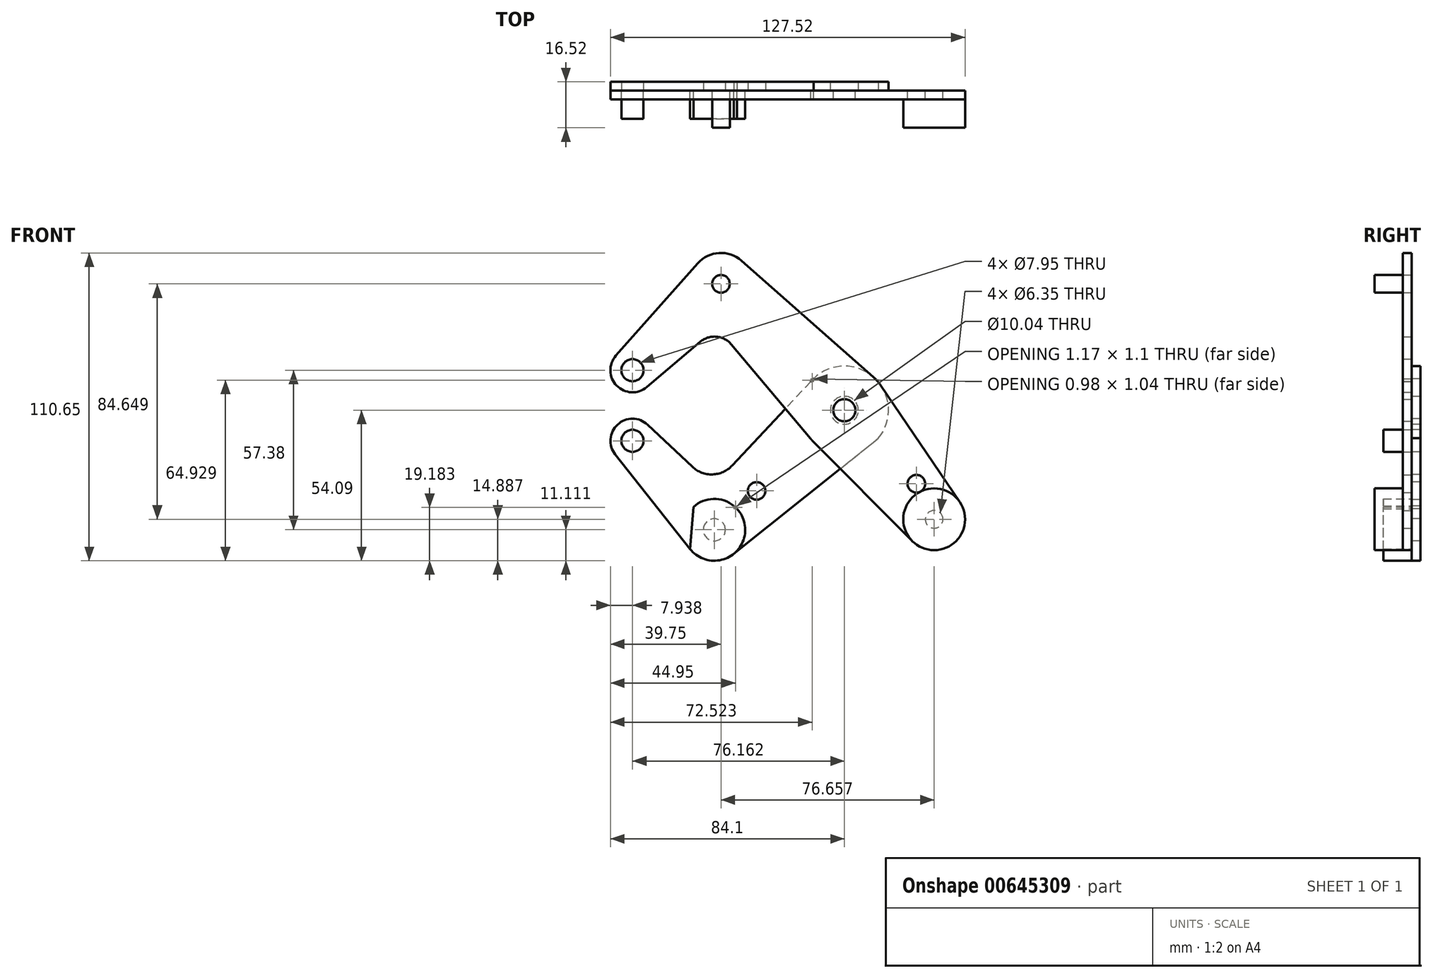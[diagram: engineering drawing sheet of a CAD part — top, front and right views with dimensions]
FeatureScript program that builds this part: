
annotation { "Feature Type Name" : "Feature", "Feature Type Description" : "" }
export const myFeature = defineFeature(function(context is Context, id is Id, definition is map)
    precondition{}
    {
        {
            var Q0;
            Q0=qCreatedBy(makeId("Front.planeOp"),FACE);
            var sketch = newSketch(context, id + "F0", { "sketchPlane" : qUnion([Q0])});
            skCircle(sketch, "E0", {"center": v(-76.16, 14.4) * mm, "radius": 7.94 * mm});
            skLineSegment(sketch, "E1", {"start": v(-76.16, 14.4) * mm, "end": v(-44.35, 45.45) * mm, "construction": true});
            skCircle(sketch, "E2", {"center": v(-44.35, 45.45) * mm, "radius": 3.18 * mm});
            skCircle(sketch, "E3", {"center": v(-44.35, 45.45) * mm, "radius": 11.11 * mm});
            skLineSegment(sketch, "E4", {"start": v(-44.35, 45.45) * mm, "end": v(0, 0) * mm, "construction": true});
            skCircle(sketch, "E5", {"center": v(0, 0) * mm, "radius": 15.88 * mm});
            skCircle(sketch, "E6", {"center": v(0, 0) * mm, "radius": 3.98 * mm});
            skCircle(sketch, "E7", {"center": v(-76.16, 14.4) * mm, "radius": 3.98 * mm});
            skCircle(sketch, "E8", {"center": v(0, 0) * mm, "radius": 5.02 * mm});
            skLineSegment(sketch, "E9", {"start": v(-82.1, 19.67) * mm, "end": v(-52.66, 52.82) * mm});
            skLineSegment(sketch, "E10", {"start": v(-71.04, 8.34) * mm, "end": v(-51.79, 24.6) * mm});
            skLineSegment(sketch, "E11", {"start": v(-40.57, 23.65) * mm, "end": v(-12.16, -10.2) * mm});
            skLineSegment(sketch, "E12", {"start": v(10.5, 11.9) * mm, "end": v(-37, 53.78) * mm});
            skLineSegment(sketch, "E13", {"start": v(0, 0) * mm, "end": v(32.3, -39.2) * mm, "construction": true});
            skCircle(sketch, "E14", {"center": v(32.3, -39.2) * mm, "radius": 11.11 * mm});
            skCircle(sketch, "E15", {"center": v(25.9, -26.43) * mm, "radius": 3.18 * mm});
            skCircle(sketch, "E16", {"center": v(32.3, -39.2) * mm, "radius": 3.18 * mm});
            skLineSegment(sketch, "E17", {"start": v(13.14, 8.9) * mm, "end": v(41.5, -32.97) * mm});
            skLineSegment(sketch, "E18", {"start": v(-11.25, -11.2) * mm, "end": v(24.43, -47.04) * mm});
            skArc(sketch, "E19", {"start": v(-40.57, 23.65) * mm, "mid": v(-45.98, 26.46) * mm, "end": v(-51.79, 24.6) * mm});
            skLineSegment(sketch, "E20.trimOffspring", {"start": v(-37.18, 36.96) * mm, "end": v(-36.57, 37.47) * mm});
            skLineSegment(sketch, "E21", {"start": v(0, 0) * mm, "end": v(-46.74, -42.98) * mm, "construction": true});
            skLineSegment(sketch, "E22", {"start": v(-46.74, -42.98) * mm, "end": v(-76.16, -10.98) * mm, "construction": true});
            skCircle(sketch, "E23", {"center": v(-76.16, -10.98) * mm, "radius": 7.94 * mm});
            skCircle(sketch, "E24", {"center": v(-76.16, -10.98) * mm, "radius": 3.98 * mm});
            skCircle(sketch, "E25", {"center": v(-46.74, -42.98) * mm, "radius": 11.11 * mm});
            skCircle(sketch, "E26", {"center": v(-46.74, -42.98) * mm, "radius": 3.98 * mm});
            skCircle(sketch, "E27", {"center": v(-31.54, -29) * mm, "radius": 3.18 * mm});
            skLineSegment(sketch, "E28", {"start": v(-70.72, -5.2) * mm, "end": v(-54.64, -20.33) * mm});
            skLineSegment(sketch, "E29", {"start": v(-39.8, -51.66) * mm, "end": v(12.27, -10.07) * mm});
            skLineSegment(sketch, "E30", {"start": v(-11.09, 11.36) * mm, "end": v(-40.34, -19.88) * mm});
            skArc(sketch, "E31", {"start": v(-54.64, -20.33) * mm, "mid": v(-47.4, -23.07) * mm, "end": v(-40.34, -19.88) * mm});
            skLineSegment(sketch, "E32.trimOffspring", {"start": v(-39.74, -34.36) * mm, "end": v(-38.56, -35.46) * mm});
            skLineSegment(sketch, "E33", {"start": v(-55.45, -49.88) * mm, "end": v(-82.38, -15.92) * mm});
            skLineSegment(sketch, "E34", {"start": v(-76.16, 14.4) * mm, "end": v(-76.16, -10.98) * mm, "construction": true});
            skLineSegment(sketch, "E35", {"start": v(-55.45, -49.88) * mm, "end": v(-54.27, -34.8) * mm});
            skSolve(sketch);
        }
        {
            var Q0;
            Q0=makeQuery(id+"F0.imprint","IMPRINT",FACE,{"disambiguationData":[TD([[makeQuery(id+"F0.imprint","IMPRINT",EDGE,{"derivedFrom":sQuery(id+"F0.wireOp",EDGE,"E7")}),-1.0]])]});
            var Q1;
            {var subQ1=sQuery(id+"F0.wireOp",EDGE,"E9");Q1=makeQuery(id+"F0.imprint","IMPRINT",FACE,{"disambiguationData":[TD([[makeQuery(id+"F0.imprint","IMPRINT",EDGE,{"derivedFrom":subQ1}),-1.0]])]});}
            var Q2;
            Q2=makeQuery(id+"F0.imprint","IMPRINT",FACE,{"disambiguationData":[TD([[makeQuery(id+"F0.imprint","IMPRINT",EDGE,{"derivedFrom":sQuery(id+"F0.wireOp",EDGE,"E2")}),-1.0]])]});
            var Q3;
            {var subQ0=sQuery(id+"F0.wireOp",EDGE,"E11");var subQ1=sQuery(id+"F0.wireOp",EDGE,"E5");var subQ2=makeQuery(id+"F0.imprint","INTERSECT",VERTEX,{"derivedFrom":[subQ1,subQ0]});Q3=makeQuery(id+"F0.imprint","IMPRINT",FACE,{"disambiguationData":[TD([[makeQuery(id+"F0.imprint","IMPRINT",EDGE,{"disambiguationData":[TD([[subQ2,1.0]])],"derivedFrom":subQ1}),-1.0]])]});}
            var Q4;
            {var subQ0=sQuery(id+"F0.wireOp",EDGE,"E18");var subQ1=sQuery(id+"F0.wireOp",EDGE,"E5");var subQ2=makeQuery(id+"F0.imprint","INTERSECT",VERTEX,{"derivedFrom":[subQ1,subQ0]});Q4=makeQuery(id+"F0.imprint","IMPRINT",FACE,{"disambiguationData":[TD([[makeQuery(id+"F0.imprint","IMPRINT",EDGE,{"disambiguationData":[TD([[subQ2,-1.0]])],"derivedFrom":subQ1}),-1.0]])]});}
            var Q5;
            {var subQ3=sQuery(id+"F0.wireOp",EDGE,"E15");Q5=makeQuery(id+"F0.imprint","IMPRINT",FACE,{"disambiguationData":[TD([[makeQuery(id+"F0.imprint","IMPRINT",EDGE,{"derivedFrom":subQ3}),-1.0]])]});}
            var Q6;
            Q6=makeQuery(id+"F0.imprint","IMPRINT",FACE,{"disambiguationData":[TD([[makeQuery(id+"F0.imprint","IMPRINT",EDGE,{"derivedFrom":sQuery(id+"F0.wireOp",EDGE,"E6")}),-1.0]])]});
            var Q7;
            Q7=makeQuery(id+"F0.imprint","IMPRINT",FACE,{"disambiguationData":[TD([[makeQuery(id+"F0.imprint","IMPRINT",EDGE,{"derivedFrom":sQuery(id+"F0.wireOp",EDGE,"E16")}),-1.0]])]});
            var Q8;
            {var subQ0=sQuery(id+"F0.wireOp",EDGE,"E29");var subQ1=sQuery(id+"F0.wireOp",EDGE,"E5");var subQ2=makeQuery(id+"F0.imprint","INTERSECT",VERTEX,{"disambiguationData":[OD(0.0)],"derivedFrom":[subQ1,subQ0]});Q8=makeQuery(id+"F0.imprint","IMPRINT",FACE,{"disambiguationData":[TD([[makeQuery(id+"F0.imprint","IMPRINT",EDGE,{"disambiguationData":[TD([[subQ2,1.0]])],"derivedFrom":subQ1}),1.0]])]});}
            var Q9;
            Q9=makeQuery(id+"F0.imprint","IMPRINT",FACE,{"disambiguationData":[TD([[makeQuery(id+"F0.imprint","IMPRINT",EDGE,{"derivedFrom":sQuery(id+"F0.wireOp",EDGE,"E8")}),-1.0]])]});
            extrude(context, id + "F1", {"entities" : qUnion([Q0, Q1, Q2, Q3, Q4, Q5, Q6, Q7, Q8, Q9]), "depth" : 3.17 * mm, "offsetDistance" : 25.4 * mm});
        }
        {
            var Q0;
            Q0=makeQuery(id+"F0.imprint","IMPRINT",FACE,{"disambiguationData":[TD([[makeQuery(id+"F0.imprint","IMPRINT",EDGE,{"derivedFrom":sQuery(id+"F0.wireOp",EDGE,"E27")}),-1.0]])]});
            var Q1;
            Q1=makeQuery(id+"F0.imprint","IMPRINT",FACE,{"disambiguationData":[TD([[makeQuery(id+"F0.imprint","IMPRINT",EDGE,{"derivedFrom":sQuery(id+"F0.wireOp",EDGE,"E24")}),-1.0]])]});
            var Q2;
            Q2=makeQuery(id+"F0.imprint","IMPRINT",FACE,{"disambiguationData":[TD([[makeQuery(id+"F0.imprint","IMPRINT",EDGE,{"derivedFrom":sQuery(id+"F0.wireOp",EDGE,"E26")}),-1.0]])]});
            var Q3;
            Q3=makeQuery(id+"F0.imprint","IMPRINT",FACE,{"disambiguationData":[TD([[makeQuery(id+"F0.imprint","IMPRINT",EDGE,{"derivedFrom":sQuery(id+"F0.wireOp",EDGE,"E8")}),-1.0]])]});
            var Q4;
            {var subQ0=sQuery(id+"F0.wireOp",EDGE,"E18");var subQ1=sQuery(id+"F0.wireOp",EDGE,"E5");var subQ2=makeQuery(id+"F0.imprint","INTERSECT",VERTEX,{"derivedFrom":[subQ1,subQ0]});Q4=makeQuery(id+"F0.imprint","IMPRINT",FACE,{"disambiguationData":[TD([[makeQuery(id+"F0.imprint","IMPRINT",EDGE,{"disambiguationData":[TD([[subQ2,-1.0]])],"derivedFrom":subQ1}),-1.0]])]});}
            var Q5;
            {var subQ0=sQuery(id+"F0.wireOp",EDGE,"E11");var subQ1=sQuery(id+"F0.wireOp",EDGE,"E5");var subQ2=makeQuery(id+"F0.imprint","INTERSECT",VERTEX,{"derivedFrom":[subQ1,subQ0]});Q5=makeQuery(id+"F0.imprint","IMPRINT",FACE,{"disambiguationData":[TD([[makeQuery(id+"F0.imprint","IMPRINT",EDGE,{"disambiguationData":[TD([[subQ2,1.0]])],"derivedFrom":subQ1}),-1.0]])]});}
            var Q6;
            {var subQ0=sQuery(id+"F0.wireOp",EDGE,"E35");Q6=makeQuery(id+"F0.imprint","IMPRINT",FACE,{"disambiguationData":[TD([[makeQuery(id+"F0.imprint","IMPRINT",EDGE,{"derivedFrom":subQ0}),1.0]])]});}
            extrude(context, id + "F2", {"entities" : qUnion([Q0, Q1, Q2, Q3, Q4, Q5, Q6]), "oppositeDirection" : true, "depth" : 3.17 * mm, "offsetDistance" : 25.4 * mm});
        }
        {
            var Q0;
            Q0=makeQuery(id+"F1.opExtrude","CAP_FACE",FACE,{"disambiguationData":[OSD([sQuery(id+"F0.wireOp",EDGE,"E0"),sQuery(id+"F0.wireOp",EDGE,"E2"),sQuery(id+"F0.wireOp",EDGE,"E3"),sQuery(id+"F0.wireOp",EDGE,"E5"),sQuery(id+"F0.wireOp",EDGE,"E6"),sQuery(id+"F0.wireOp",EDGE,"E7"),sQuery(id+"F0.wireOp",EDGE,"E9"),sQuery(id+"F0.wireOp",EDGE,"E10"),sQuery(id+"F0.wireOp",EDGE,"E11"),sQuery(id+"F0.wireOp",EDGE,"E12"),sQuery(id+"F0.wireOp",EDGE,"E14"),sQuery(id+"F0.wireOp",EDGE,"E15"),sQuery(id+"F0.wireOp",EDGE,"E16"),sQuery(id+"F0.wireOp",EDGE,"E17"),sQuery(id+"F0.wireOp",EDGE,"E18"),sQuery(id+"F0.wireOp",EDGE,"E19"),sQuery(id+"F0.wireOp",EDGE,"E30")])],"isStart":false});
            var sketch = newSketch(context, id + "F3", { "sketchPlane" : qUnion([Q0])});
            skCircle(sketch, "E36", {"center": v(-44.35, 45.45) * mm, "radius": 3.98 * mm});
            skCircle(sketch, "E37.0", {"center": v(32.3, -39.2) * mm, "radius": 11.11 * mm});
            skSolve(sketch);
        }
        {
            var Q0;
            Q0=makeQuery(id+"F0.imprint","IMPRINT",FACE,{"disambiguationData":[TD([[makeQuery(id+"F0.imprint","IMPRINT",EDGE,{"derivedFrom":sQuery(id+"F0.wireOp",EDGE,"E24")}),1.0]])]});
            var Q1;
            Q1=makeQuery(id+"F3.imprint","IMPRINT",FACE,{"disambiguationData":[TD([[makeQuery(id+"F3.imprint","IMPRINT",EDGE,{"derivedFrom":makeQuery(id+"F1.opExtrude","CAP_EDGE",EDGE,{"disambiguationData":[OSD([sQuery(id+"F0.wireOp",EDGE,"E16")])],"isStart":false})}),1.0]])]});
            var Q2;
            Q2=makeQuery(id+"F3.imprint","IMPRINT",FACE,{"disambiguationData":[TD([[makeQuery(id+"F3.imprint","IMPRINT",EDGE,{"derivedFrom":makeQuery(id+"F1.opExtrude","CAP_EDGE",EDGE,{"disambiguationData":[OSD([sQuery(id+"F0.wireOp",EDGE,"E2")])],"isStart":false})}),1.0]])]});
            var Q3;
            Q3=makeQuery(id+"F3.imprint","IMPRINT",FACE,{"disambiguationData":[TD([[makeQuery(id+"F3.imprint","IMPRINT",EDGE,{"derivedFrom":makeQuery(id+"F1.opExtrude","CAP_EDGE",EDGE,{"disambiguationData":[OSD([sQuery(id+"F0.wireOp",EDGE,"E16")])],"isStart":false})}),-1.0]])]});
            var Q4;
            Q4=makeQuery(id+"F0.imprint","IMPRINT",FACE,{"disambiguationData":[TD([[makeQuery(id+"F0.imprint","IMPRINT",EDGE,{"derivedFrom":sQuery(id+"F0.wireOp",EDGE,"E26")}),1.0]])]});
            var Q5;
            Q5=makeQuery(id+"F0.imprint","IMPRINT",FACE,{"disambiguationData":[TD([[makeQuery(id+"F0.imprint","IMPRINT",EDGE,{"derivedFrom":sQuery(id+"F0.wireOp",EDGE,"E26")}),-1.0]])]});
            extrude(context, id + "F4", {"entities" : qUnion([Q0, Q1, Q2, Q3, Q4, Q5]), "depth" : 10.16 * mm, "offsetDistance" : 25.4 * mm});
        }
    });
